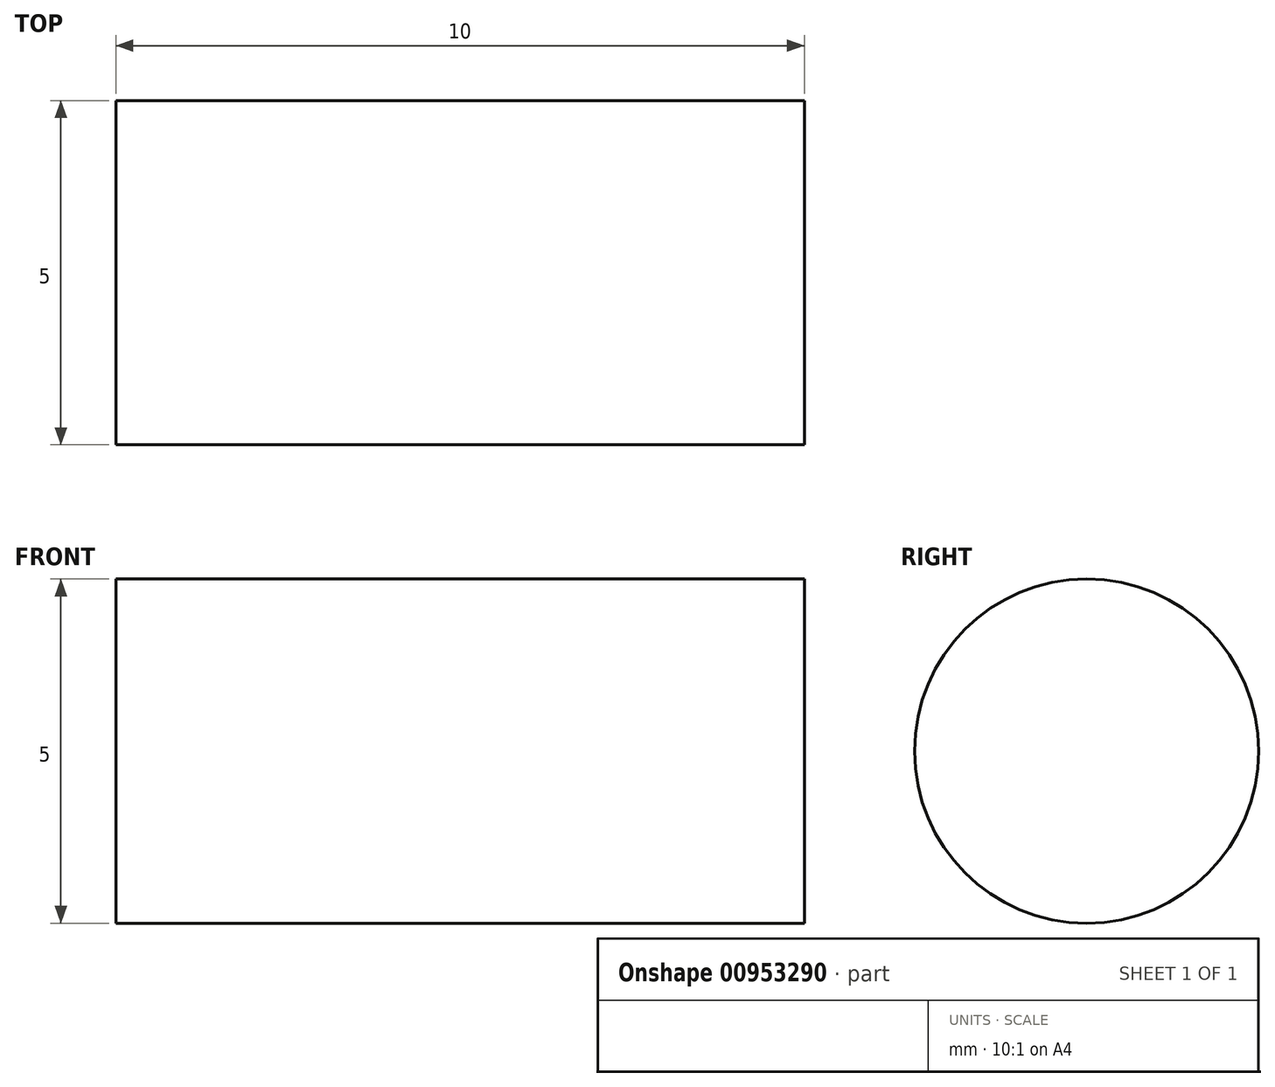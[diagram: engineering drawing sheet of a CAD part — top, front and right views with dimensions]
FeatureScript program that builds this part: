
annotation { "Feature Type Name" : "Feature", "Feature Type Description" : "" }
export const myFeature = defineFeature(function(context is Context, id is Id, definition is map)
    precondition{}
    {
        {
            var Q0;
            Q0=qCreatedBy(makeId("Right.planeOp"),FACE);
            var sketch = newSketch(context, id + "F0", { "sketchPlane" : qUnion([Q0])});
            skCircle(sketch, "E0", {"center": v(0, 0) * mm, "radius": 2.5 * mm});
            skSolve(sketch);
        }
        {
            var Q0;
            Q0 = qSketchRegion(id + "F0", true);
            extrude(context, id + "F1", {"entities" : qUnion([Q0]), "depth" : 10 * mm, "offsetDistance" : 25 * mm});
        }
    });
